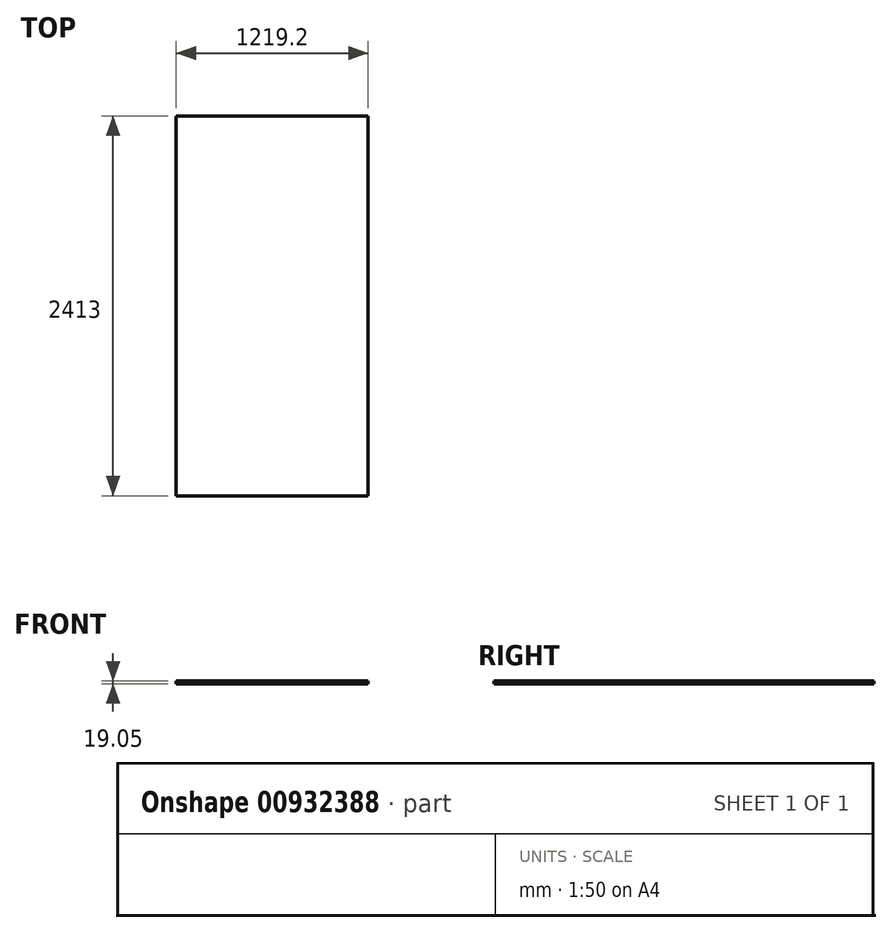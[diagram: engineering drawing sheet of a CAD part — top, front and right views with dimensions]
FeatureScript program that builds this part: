
annotation { "Feature Type Name" : "Feature", "Feature Type Description" : "" }
export const myFeature = defineFeature(function(context is Context, id is Id, definition is map)
    precondition{}
    {
        {
            var Q0;
            Q0=qCreatedBy(makeId("Top.planeOp"),FACE);
            var sketch = newSketch(context, id + "F0", { "sketchPlane" : qUnion([Q0])});
            skLineSegment(sketch, "E0.bottom", {"start": v(609.6, 1206.5) * mm, "end": v(-609.6, 1206.5) * mm});
            skLineSegment(sketch, "E0.top", {"start": v(609.6, -1206.5) * mm, "end": v(-609.6, -1206.5) * mm});
            skLineSegment(sketch, "E0.left", {"start": v(609.6, 1206.5) * mm, "end": v(609.6, -1206.5) * mm});
            skLineSegment(sketch, "E0.right", {"start": v(-609.6, 1206.5) * mm, "end": v(-609.6, -1206.5) * mm});
            skPoint(sketch, "E0.middle", {"position": v(0, 0) * mm});
            skSolve(sketch);
        }
        {
            var Q0;
            Q0=makeQuery(id+"F0.imprint","IMPRINT",FACE,{"disambiguationData":[TD([[makeQuery(id+"F0.imprint","IMPRINT",EDGE,{"derivedFrom":sQuery(id+"F0.wireOp",EDGE,"E0.bottom")}),1.0]])]});
            extrude(context, id + "F1", {"entities" : qUnion([Q0]), "depth" : 19.05 * mm, "offsetDistance" : 25.4 * mm});
        }
    });
